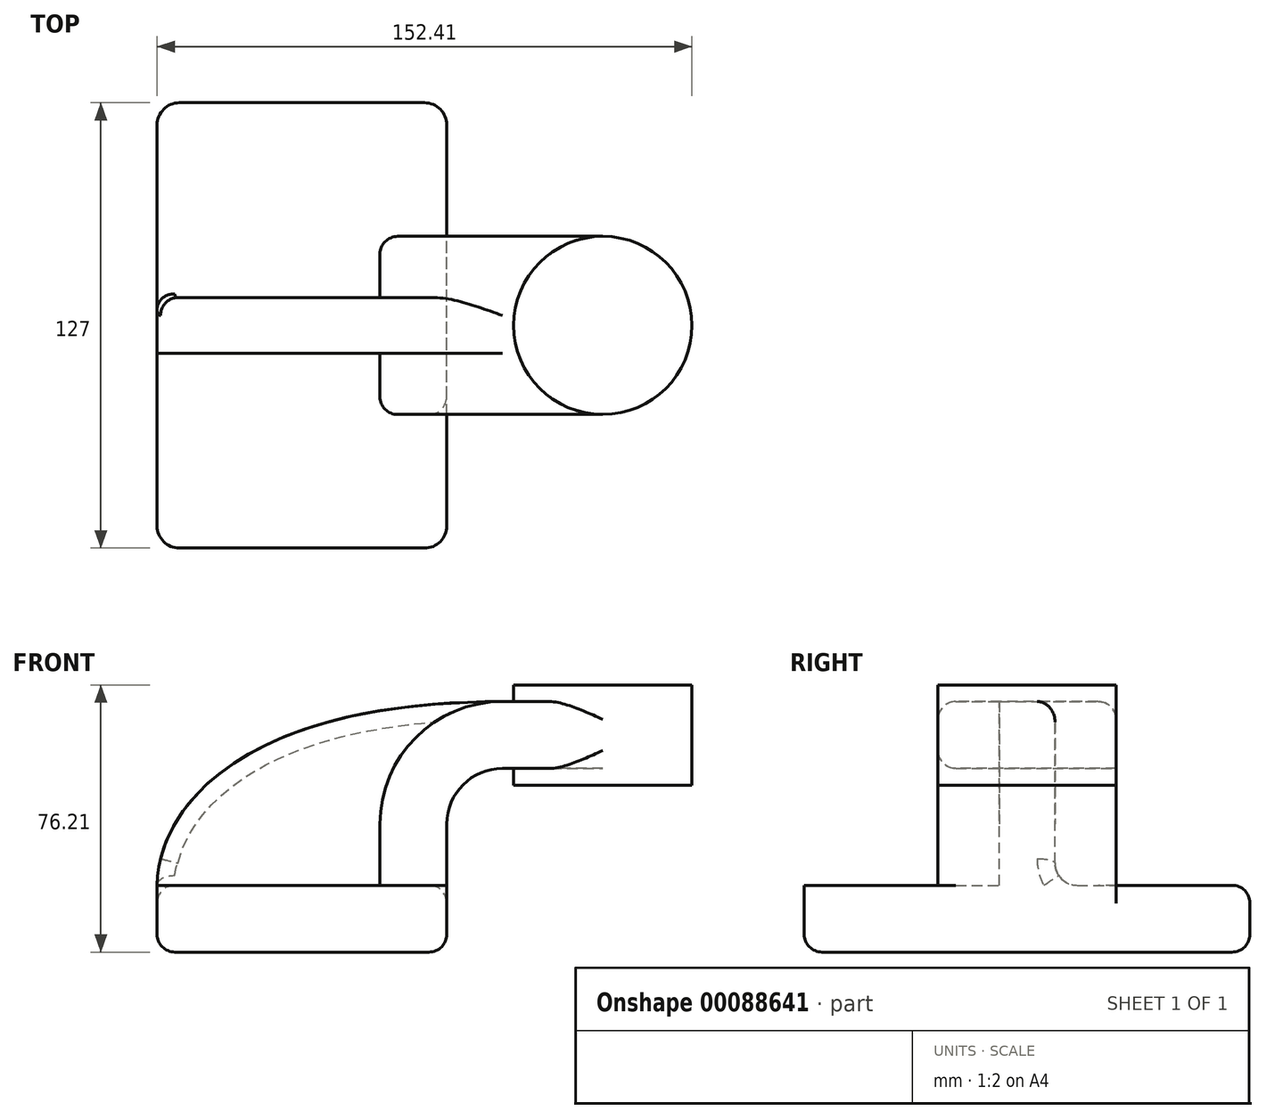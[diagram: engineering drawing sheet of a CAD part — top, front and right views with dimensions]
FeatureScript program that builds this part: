
annotation { "Feature Type Name" : "Feature", "Feature Type Description" : "" }
export const myFeature = defineFeature(function(context is Context, id is Id, definition is map)
    precondition{}
    {
        {
            var Q0;
            Q0=qCreatedBy(makeId("Front.planeOp"),FACE);
            var sketch = newSketch(context, id + "F0", { "sketchPlane" : qUnion([Q0])});
            skLineSegment(sketch, "E0.bottom", {"start": v(-41.28, 9.53) * mm, "end": v(41.28, 9.53) * mm});
            skLineSegment(sketch, "E0.top", {"start": v(-41.27, -9.53) * mm, "end": v(41.28, -9.53) * mm});
            skLineSegment(sketch, "E0.left", {"start": v(-41.28, 9.52) * mm, "end": v(-41.28, -9.53) * mm});
            skLineSegment(sketch, "E0.right", {"start": v(41.27, 9.53) * mm, "end": v(41.27, -9.52) * mm});
            skPoint(sketch, "E0.middle", {"position": v(0, 0) * mm});
            skLineSegment(sketch, "E1.bottom", {"start": v(60.33, 66.67) * mm, "end": v(111.13, 66.67) * mm});
            skLineSegment(sketch, "E1.top", {"start": v(60.33, 38.1) * mm, "end": v(111.13, 38.1) * mm});
            skLineSegment(sketch, "E1.left", {"start": v(60.33, 66.67) * mm, "end": v(60.33, 38.1) * mm});
            skLineSegment(sketch, "E1.right", {"start": v(111.13, 66.67) * mm, "end": v(111.13, 38.1) * mm});
            skPoint(sketch, "E1.middle", {"position": v(85.73, 52.39) * mm});
            skLineSegment(sketch, "E2", {"start": v(41.27, 9.52) * mm, "end": v(41.27, 26.99) * mm});
            skArc(sketch, "E3.filletArc", {"start": v(57.15, 42.86) * mm, "mid": v(45.92, 38.21) * mm, "end": v(41.28, 26.99) * mm});
            skLineSegment(sketch, "E4", {"start": v(57.15, 42.86) * mm, "end": v(85.73, 42.86) * mm});
            skLineSegment(sketch, "E5.0", {"start": v(22.23, 9.52) * mm, "end": v(22.23, 26.99) * mm});
            skArc(sketch, "E5.1", {"start": v(57.15, 61.91) * mm, "mid": v(32.45, 51.68) * mm, "end": v(22.23, 26.99) * mm});
            skLineSegment(sketch, "E5.2", {"start": v(57.15, 61.91) * mm, "end": v(85.73, 61.91) * mm});
            skLineSegment(sketch, "E6", {"start": v(85.73, 66.67) * mm, "end": v(85.73, 38.1) * mm});
            skFitSpline(sketch, "E7", {"points": [v(-41.28, 9.52) * mm, v(57.15, 61.91) * mm], "startDerivative": vector(0, 57.63) * mm, "endDerivative": vector(235.19, 0) * mm});
            skSolve(sketch);
        }
        {
            var Q0;
            Q0=makeQuery(id+"F0.imprint","IMPRINT",FACE,{"disambiguationData":[TD([[makeQuery(id+"F0.imprint","IMPRINT",EDGE,{"derivedFrom":sQuery(id+"F0.wireOp",EDGE,"E0.top")}),1.0]])]});
            extrude(context, id + "F1", {"entities" : qUnion([Q0]), "endBound" : BoundingType.SYMMETRIC, "depth" : 127 * mm});
        }
        {
            var Q0;
            {var subQ2=sQuery(id+"F0.wireOp",EDGE,"E2");Q0=makeQuery(id+"F0.imprint","IMPRINT",FACE,{"disambiguationData":[TD([[makeQuery(id+"F0.imprint","IMPRINT",EDGE,{"derivedFrom":subQ2}),1.0]])]});}
            var Q1;
            {var subQ0=sQuery(id+"F0.wireOp",EDGE,"E5.2");var subQ1=sQuery(id+"F0.wireOp",EDGE,"E1.left");var subQ2=makeQuery(id+"F0.imprint","INTERSECT",VERTEX,{"derivedFrom":[subQ1,subQ0]});Q1=makeQuery(id+"F0.imprint","IMPRINT",FACE,{"disambiguationData":[TD([[makeQuery(id+"F0.imprint","IMPRINT",EDGE,{"disambiguationData":[TD([[subQ2,-1.0]])],"derivedFrom":subQ1}),1.0]])]});}
            extrude(context, id + "F2", {"entities" : qUnion([Q0, Q1]), "operationType" : NewBodyOperationType.ADD, "endBound" : BoundingType.SYMMETRIC, "depth" : 50.8 * mm});
        }
        {
            var Q0;
            {var subQ2=sQuery(id+"F0.wireOp",EDGE,"E5.0");Q0=makeQuery(id+"F0.imprint","IMPRINT",FACE,{"disambiguationData":[TD([[makeQuery(id+"F0.imprint","IMPRINT",EDGE,{"derivedFrom":subQ2}),1.0]])]});}
            extrude(context, id + "F3", {"entities" : qUnion([Q0]), "operationType" : NewBodyOperationType.ADD, "endBound" : BoundingType.SYMMETRIC, "depth" : 15.88 * mm});
        }
        {
            var Q0;
            {var subQ0=sQuery(id+"F0.wireOp",EDGE,"E1.right");Q0=makeQuery(id+"F0.imprint","IMPRINT",FACE,{"disambiguationData":[TD([[makeQuery(id+"F0.imprint","IMPRINT",EDGE,{"derivedFrom":subQ0}),-1.0]])]});}
            var Q1;
            Q1=sQuery(id+"F0.wireOp",EDGE,"E6");
            revolve(context, id + "F4", {"operationType" : NewBodyOperationType.ADD, "entities" : qUnion([Q0]), "axis" : qUnion([Q1]), "revolveType" : RevolveType.FULL});
        }
        {
            var Q0;
            Q0=makeQuery(id+"F1.opExtrude","CAP_EDGE",EDGE,{"disambiguationData":[OSD([sQuery(id+"F0.wireOp",EDGE,"E0.left")])],"isStart":false});
            var Q1;
            Q1=makeQuery(id+"F1.opExtrude","CAP_EDGE",EDGE,{"disambiguationData":[OSD([sQuery(id+"F0.wireOp",EDGE,"E0.right")])],"isStart":false});
            var Q2;
            Q2=makeQuery(id+"F2.opExtrude","CAP_EDGE",EDGE,{"disambiguationData":[OSD([sQuery(id+"F0.wireOp",EDGE,"E0.bottom")])],"isStart":false});
            var Q3;
            Q3=makeQuery(id+"F3.opExtrude","CAP_EDGE",EDGE,{"disambiguationData":[OSD([sQuery(id+"F0.wireOp",EDGE,"E0.bottom")])],"isStart":false});
            var Q4;
            Q4=makeQuery(id+"F2.opExtrude","CAP_EDGE",EDGE,{"disambiguationData":[OSD([sQuery(id+"F0.wireOp",EDGE,"E0.bottom")])],"isStart":true});
            var Q5;
            Q5=makeQuery(id+"F3.opExtrude","CAP_EDGE",EDGE,{"disambiguationData":[OSD([sQuery(id+"F0.wireOp",EDGE,"E0.bottom")])],"isStart":true});
            var Q6;
            Q6=makeQuery(id+"F1.opExtrude","CAP_EDGE",EDGE,{"disambiguationData":[OSD([sQuery(id+"F0.wireOp",EDGE,"E0.right")])],"isStart":true});
            var Q7;
            Q7=makeQuery(id+"F1.opExtrude","CAP_EDGE",EDGE,{"disambiguationData":[OSD([sQuery(id+"F0.wireOp",EDGE,"E0.left")])],"isStart":true});
            fillet(context, id + "F5", {"entities" : qUnion([Q0, Q1, Q2, Q3, Q4, Q5, Q6, Q7]), "radius" : 6.35 * mm, "tangentPropagation" : true, "allowEdgeOverflow" : false});
        }
        {
            var Q0;
            Q0=makeQuery(id+"F3.opExtrude","CAP_EDGE",EDGE,{"disambiguationData":[OSD([sQuery(id+"F0.wireOp",EDGE,"E7")])],"isStart":true});
            var Q1;
            Q1=makeQuery(id+"F2.opExtrude","CAP_EDGE",EDGE,{"disambiguationData":[OSD([sQuery(id+"F0.wireOp",EDGE,"E5.2")])],"isStart":true});
            var Q2;
            Q2=makeQuery(id+"F2.opExtrude","CAP_EDGE",EDGE,{"disambiguationData":[OSD([sQuery(id+"F0.wireOp",EDGE,"E5.2")])],"isStart":false});
            var Q3;
            Q3=makeQuery(id+"F2.opExtrude","CAP_EDGE",EDGE,{"disambiguationData":[OSD([sQuery(id+"F0.wireOp",EDGE,"E4")])],"isStart":false});
            var Q4;
            Q4=makeQuery(id+"F1.opExtrude","CAP_EDGE",EDGE,{"disambiguationData":[OSD([sQuery(id+"F0.wireOp",EDGE,"E0.top")])],"isStart":false});
            fillet(context, id + "F6", {"entities" : qUnion([Q0, Q1, Q2, Q3, Q4]), "radius" : 5.08 * mm, "tangentPropagation" : true, "allowEdgeOverflow" : false});
        }
    });
